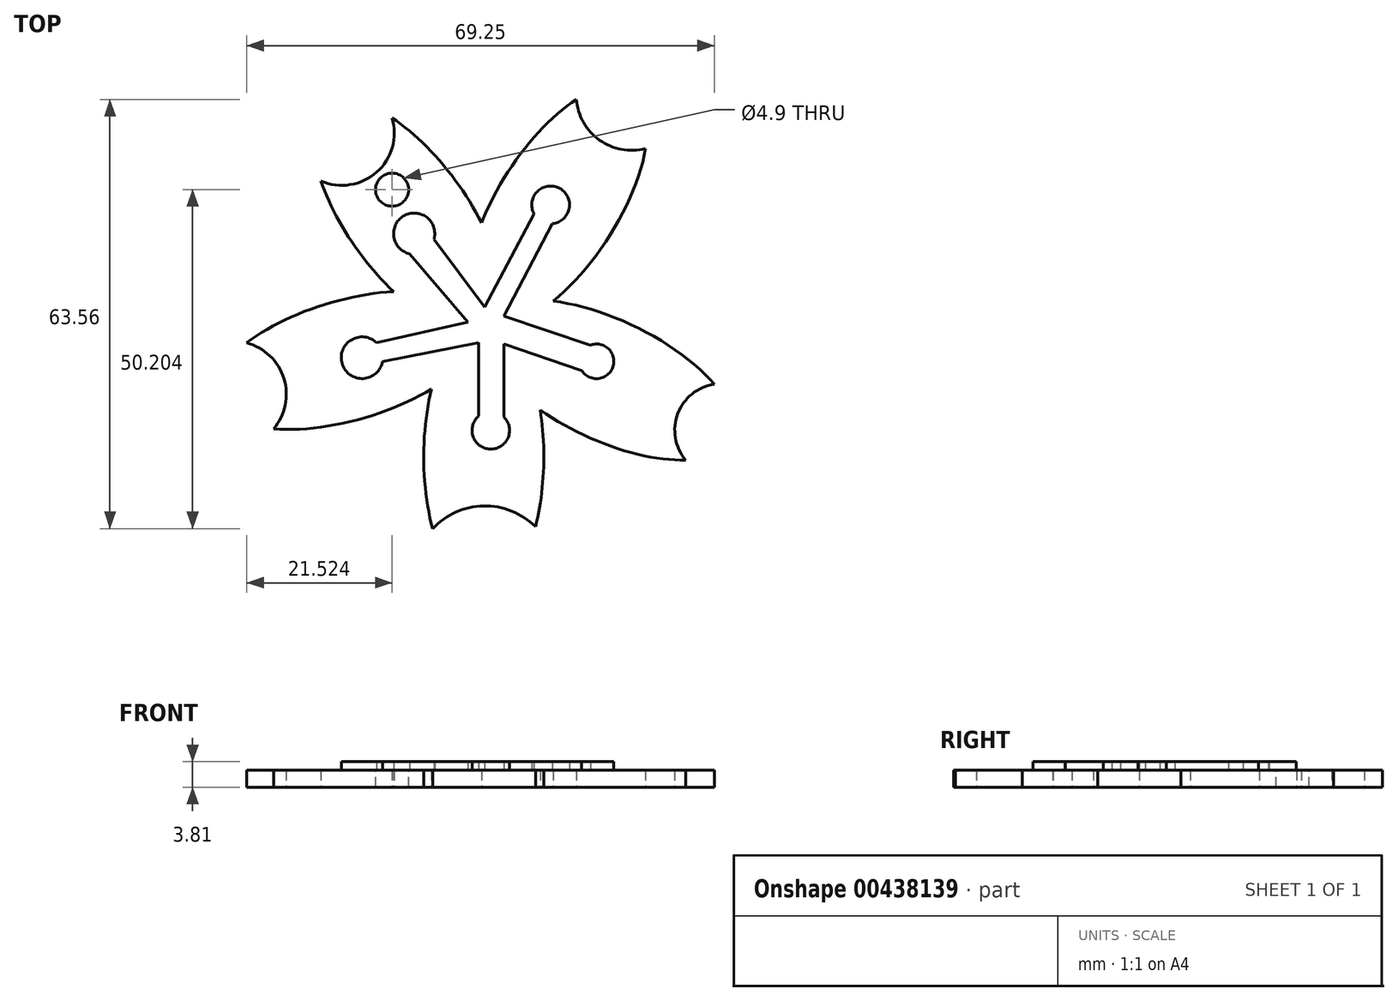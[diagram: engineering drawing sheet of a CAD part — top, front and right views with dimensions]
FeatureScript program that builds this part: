
annotation { "Feature Type Name" : "Feature", "Feature Type Description" : "" }
export const myFeature = defineFeature(function(context is Context, id is Id, definition is map)
    precondition{}
    {
        {
            var Q0;
            Q0=qCreatedBy(makeId("Top.planeOp"),FACE);
            var sketch = newSketch(context, id + "F0", { "sketchPlane" : qUnion([Q0])});
            skPoint(sketch, "E0.0.midPoint", {"position": v(-18.42, 2.19) * mm});
            skEllipticalArc(sketch, "E1", {});
            skArc(sketch, "E2", {"start": v(-10.76, -19.54) * mm, "mid": v(-18.44, -16.48) * mm, "end": v(-26, -19.84) * mm});
            skEllipticalArc(sketch, "E3", {});
            skArc(sketch, "E4", {"start": v(15.73, 1.54) * mm, "mid": v(10.31, -2.82) * mm, "end": v(11.48, -9.67) * mm});
            skEllipticalArc(sketch, "E5", {});
            skArc(sketch, "E6", {"start": v(-4.7, 43.72) * mm, "mid": v(-1.27, 37.7) * mm, "end": v(5.54, 36.44) * mm});
            skEllipticalArc(sketch, "E7", {});
            skArc(sketch, "E8", {"start": v(-42.53, 31.66) * mm, "mid": v(-34.28, 32.96) * mm, "end": v(-32, 41) * mm});
            skEllipticalArc(sketch, "E9", {});
            skArc(sketch, "E10", {"start": v(-49.56, -5.06) * mm, "mid": v(-48.02, 2.4) * mm, "end": v(-53.52, 7.67) * mm});
            skPoint(sketch, "E0.cCircle.center.orphan", {"position": v(-18.42, 10.93) * mm});
            skPoint(sketch, "E11.trimOffspring.end.orphan", {"position": v(-12.07, 2.19) * mm});
            skPoint(sketch, "E12.trimOffspring.end.orphan", {"position": v(-24.77, 2.19) * mm});
            const initialGuessF0  = {"E1": [-0.018419569358229637, -0.009209784679114819, 0, -1, 0.02032, 0.00889, 1.0375960775229152, 5.262947220574454], "E3": [-7.52416357180769e-05, 0.002189779299485402, -0.902772033588167, 0.4301193501472418, 0.02032, 0.00889, 3.914449507509073, 2.4409470220273937], "E5": [-0.0074550958280823094, 0.028037776911064273, -0.5395902327828408, -0.8419277764068362, 0.02032, 0.00889, 3.9042333142509738, 2.3368799745310973], "E7": [-0.029716556891798973, 0.026384949684143066, 0.5901133935646233, -0.8073203718076511, 0.02032, 0.00889, 4.0918939551895885, 2.2747363454446012], "E9": [-0.038638535887002945, 0.005087323021143675, 0.9606958523615047, 0.2776030966243028, 0.02032, 0.00889, 3.9984789776767142, 2.3025399142686345]};
            skSetInitialGuess(sketch, initialGuessF0);
            skSolve(sketch);
        }
        {
            var Q0;
            {var subQ0=sQuery(id+"F0.wireOp",EDGE,"E6");Q0=makeQuery(id+"F0.imprint","IMPRINT",FACE,{"disambiguationData":[TD([[makeQuery(id+"F0.imprint","IMPRINT",EDGE,{"derivedFrom":subQ0}),-1.0]])]});}
            var Q1;
            {var subQ0=sQuery(id+"F0.wireOp",EDGE,"E3");var subQ1=sQuery(id+"F0.wireOp",EDGE,"E1");var subQ2=makeQuery(id+"F0.imprint","INTERSECT",VERTEX,{"disambiguationData":[OD(1.0)],"derivedFrom":[subQ1,subQ0]});Q1=makeQuery(id+"F0.imprint","IMPRINT",FACE,{"disambiguationData":[TD([[makeQuery(id+"F0.imprint","IMPRINT",EDGE,{"disambiguationData":[TD([[subQ2,-1.0]])],"derivedFrom":subQ1}),-1.0]])]});}
            var Q2;
            {var subQ0=sQuery(id+"F0.wireOp",EDGE,"E8");Q2=makeQuery(id+"F0.imprint","IMPRINT",FACE,{"disambiguationData":[TD([[makeQuery(id+"F0.imprint","IMPRINT",EDGE,{"derivedFrom":subQ0}),-1.0]])]});}
            var Q3;
            {var subQ0=sQuery(id+"F0.wireOp",EDGE,"E10");Q3=makeQuery(id+"F0.imprint","IMPRINT",FACE,{"disambiguationData":[TD([[makeQuery(id+"F0.imprint","IMPRINT",EDGE,{"derivedFrom":subQ0}),-1.0]])]});}
            var Q4;
            {var subQ5=sQuery(id+"F0.wireOp",EDGE,"E2");Q4=makeQuery(id+"F0.imprint","IMPRINT",FACE,{"disambiguationData":[TD([[makeQuery(id+"F0.imprint","IMPRINT",EDGE,{"derivedFrom":subQ5}),-1.0]])]});}
            var Q5;
            {var subQ0=sQuery(id+"F0.wireOp",EDGE,"E4");Q5=makeQuery(id+"F0.imprint","IMPRINT",FACE,{"disambiguationData":[TD([[makeQuery(id+"F0.imprint","IMPRINT",EDGE,{"derivedFrom":subQ0}),-1.0]])]});}
            var Q6;
            {var subQ0=sQuery(id+"F0.wireOp",EDGE,"E3");var subQ1=sQuery(id+"F0.wireOp",EDGE,"E1");var subQ2=makeQuery(id+"F0.imprint","INTERSECT",VERTEX,{"disambiguationData":[OD(0.0)],"derivedFrom":[subQ1,subQ0]});Q6=makeQuery(id+"F0.imprint","IMPRINT",FACE,{"disambiguationData":[TD([[makeQuery(id+"F0.imprint","IMPRINT",EDGE,{"disambiguationData":[TD([[subQ2,-1.0]])],"derivedFrom":subQ1}),1.0]])]});}
            var Q7;
            {var subQ0=sQuery(id+"F0.wireOp",EDGE,"E5");var subQ1=sQuery(id+"F0.wireOp",EDGE,"E1");var subQ2=makeQuery(id+"F0.imprint","INTERSECT",VERTEX,{"disambiguationData":[OD(0.0)],"derivedFrom":[subQ1,subQ0]});Q7=makeQuery(id+"F0.imprint","IMPRINT",FACE,{"disambiguationData":[TD([[makeQuery(id+"F0.imprint","IMPRINT",EDGE,{"disambiguationData":[TD([[subQ2,-1.0]])],"derivedFrom":subQ1}),-1.0]])]});}
            var Q8;
            {var subQ0=sQuery(id+"F0.wireOp",EDGE,"E9");var subQ1=sQuery(id+"F0.wireOp",EDGE,"E1");var subQ2=makeQuery(id+"F0.imprint","INTERSECT",VERTEX,{"disambiguationData":[OD(1.0)],"derivedFrom":[subQ1,subQ0]});Q8=makeQuery(id+"F0.imprint","IMPRINT",FACE,{"disambiguationData":[TD([[makeQuery(id+"F0.imprint","IMPRINT",EDGE,{"disambiguationData":[TD([[subQ2,1.0]])],"derivedFrom":subQ1}),1.0]])]});}
            var Q9;
            {var subQ0=sQuery(id+"F0.wireOp",EDGE,"E9");var subQ1=sQuery(id+"F0.wireOp",EDGE,"E1");var subQ2=makeQuery(id+"F0.imprint","INTERSECT",VERTEX,{"disambiguationData":[OD(0.0)],"derivedFrom":[subQ1,subQ0]});Q9=makeQuery(id+"F0.imprint","IMPRINT",FACE,{"disambiguationData":[TD([[makeQuery(id+"F0.imprint","IMPRINT",EDGE,{"disambiguationData":[TD([[subQ2,-1.0]])],"derivedFrom":subQ1}),-1.0]])]});}
            var Q10;
            {var subQ0=sQuery(id+"F0.wireOp",EDGE,"E9");var subQ1=sQuery(id+"F0.wireOp",EDGE,"E1");var subQ2=makeQuery(id+"F0.imprint","INTERSECT",VERTEX,{"disambiguationData":[OD(0.0)],"derivedFrom":[subQ1,subQ0]});Q10=makeQuery(id+"F0.imprint","IMPRINT",FACE,{"disambiguationData":[TD([[makeQuery(id+"F0.imprint","IMPRINT",EDGE,{"disambiguationData":[TD([[subQ2,-1.0]])],"derivedFrom":subQ1}),1.0]])]});}
            var Q11;
            {var subQ0=sQuery(id+"F0.wireOp",EDGE,"E7");var subQ1=sQuery(id+"F0.wireOp",EDGE,"E1");var subQ2=makeQuery(id+"F0.imprint","INTERSECT",VERTEX,{"disambiguationData":[OD(0.0)],"derivedFrom":[subQ1,subQ0]});Q11=makeQuery(id+"F0.imprint","IMPRINT",FACE,{"disambiguationData":[TD([[makeQuery(id+"F0.imprint","IMPRINT",EDGE,{"disambiguationData":[TD([[subQ2,-1.0]])],"derivedFrom":subQ1}),-1.0]])]});}
            var Q12;
            {var subQ0=sQuery(id+"F0.wireOp",EDGE,"E7");var subQ1=sQuery(id+"F0.wireOp",EDGE,"E1");var subQ2=makeQuery(id+"F0.imprint","INTERSECT",VERTEX,{"disambiguationData":[OD(0.0)],"derivedFrom":[subQ1,subQ0]});Q12=makeQuery(id+"F0.imprint","IMPRINT",FACE,{"disambiguationData":[TD([[makeQuery(id+"F0.imprint","IMPRINT",EDGE,{"disambiguationData":[TD([[subQ2,-1.0]])],"derivedFrom":subQ1}),1.0]])]});}
            var Q13;
            {var subQ0=sQuery(id+"F0.wireOp",EDGE,"E5");var subQ1=sQuery(id+"F0.wireOp",EDGE,"E3");var subQ2=makeQuery(id+"F0.imprint","INTERSECT",VERTEX,{"disambiguationData":[OD(0.0)],"derivedFrom":[subQ1,subQ0]});Q13=makeQuery(id+"F0.imprint","IMPRINT",FACE,{"disambiguationData":[TD([[makeQuery(id+"F0.imprint","IMPRINT",EDGE,{"disambiguationData":[TD([[subQ2,-1.0]])],"derivedFrom":subQ1}),1.0]])]});}
            var Q14;
            {var subQ3=sQuery(id+"F0.wireOp",EDGE,"E9");var subQ7=sQuery(id+"F0.wireOp",EDGE,"E1");var subQ9=makeQuery(id+"F0.imprint","INTERSECT",VERTEX,{"disambiguationData":[OD(0.0)],"derivedFrom":[subQ7,subQ3]});Q14=makeQuery(id+"F0.imprint","IMPRINT",FACE,{"disambiguationData":[TD([[makeQuery(id+"F0.imprint","IMPRINT",EDGE,{"disambiguationData":[TD([[subQ9,1.0]])],"derivedFrom":subQ7}),1.0]])]});}
            var Q15;
            {var subQ0=sQuery(id+"F0.wireOp",EDGE,"E5");var subQ1=sQuery(id+"F0.wireOp",EDGE,"E1");var subQ2=makeQuery(id+"F0.imprint","INTERSECT",VERTEX,{"disambiguationData":[OD(0.0)],"derivedFrom":[subQ1,subQ0]});Q15=makeQuery(id+"F0.imprint","IMPRINT",FACE,{"disambiguationData":[TD([[makeQuery(id+"F0.imprint","IMPRINT",EDGE,{"disambiguationData":[TD([[subQ2,-1.0]])],"derivedFrom":subQ1}),1.0]])]});}
            var Q16;
            {var subQ0=sQuery(id+"F0.wireOp",EDGE,"E3");var subQ1=sQuery(id+"F0.wireOp",EDGE,"E1");var subQ2=makeQuery(id+"F0.imprint","INTERSECT",VERTEX,{"disambiguationData":[OD(1.0)],"derivedFrom":[subQ1,subQ0]});Q16=makeQuery(id+"F0.imprint","IMPRINT",FACE,{"disambiguationData":[TD([[makeQuery(id+"F0.imprint","IMPRINT",EDGE,{"disambiguationData":[TD([[subQ2,-1.0]])],"derivedFrom":subQ1}),1.0]])]});}
            extrude(context, id + "F1", {"entities" : qUnion([Q0, Q1, Q2, Q3, Q4, Q5, Q6, Q7, Q8, Q9, Q10, Q11, Q12, Q13, Q14, Q15, Q16]), "depth" : 2.54 * mm});
        }
        {
            var Q0;
            Q0=makeQuery(id+"F1.opExtrude","CAP_FACE",FACE,{"disambiguationData":[OSD([sQuery(id+"F0.wireOp",EDGE,"E1"),sQuery(id+"F0.wireOp",EDGE,"E2"),sQuery(id+"F0.wireOp",EDGE,"E3"),sQuery(id+"F0.wireOp",EDGE,"E4"),sQuery(id+"F0.wireOp",EDGE,"E5"),sQuery(id+"F0.wireOp",EDGE,"E6"),sQuery(id+"F0.wireOp",EDGE,"E7"),sQuery(id+"F0.wireOp",EDGE,"E8"),sQuery(id+"F0.wireOp",EDGE,"E9"),sQuery(id+"F0.wireOp",EDGE,"E10")])],"isStart":false});
            var sketch = newSketch(context, id + "F2", { "sketchPlane" : qUnion([Q0])});
            skCircle(sketch, "E13", {"center": v(-32, 30.36) * mm, "radius": 2.45 * mm});
            skPoint(sketch, "E14.center.orphan", {"position": v(-32, 30.78) * mm});
            skSolve(sketch);
        }
        {
            var Q0;
            Q0=makeQuery(id+"F2.imprint","IMPRINT",FACE,{"disambiguationData":[TD([[makeQuery(id+"F2.imprint","IMPRINT",EDGE,{"derivedFrom":sQuery(id+"F2.wireOp",EDGE,"E13")}),1.0]])]});
            extrude(context, id + "F3", {"entities" : qUnion([Q0]), "operationType" : NewBodyOperationType.REMOVE, "oppositeDirection" : true, "depth" : 25.4 * mm});
        }
        {
            var Q0;
            Q0=makeQuery(id+"F1.opExtrude","CAP_FACE",FACE,{"disambiguationData":[OSD([sQuery(id+"F0.wireOp",EDGE,"E1"),sQuery(id+"F0.wireOp",EDGE,"E2"),sQuery(id+"F0.wireOp",EDGE,"E3"),sQuery(id+"F0.wireOp",EDGE,"E4"),sQuery(id+"F0.wireOp",EDGE,"E5"),sQuery(id+"F0.wireOp",EDGE,"E6"),sQuery(id+"F0.wireOp",EDGE,"E7"),sQuery(id+"F0.wireOp",EDGE,"E8"),sQuery(id+"F0.wireOp",EDGE,"E9"),sQuery(id+"F0.wireOp",EDGE,"E10")])],"isStart":false});
            var sketch = newSketch(context, id + "F4", { "sketchPlane" : qUnion([Q0])});
            skLineSegment(sketch, "E15", {"start": v(-10.96, 26.77) * mm, "end": v(-18.3, 12.95) * mm});
            skLineSegment(sketch, "E16", {"start": v(-8.23, 25.33) * mm, "end": v(-15.42, 11.66) * mm});
            skLineSegment(sketch, "E17", {"start": v(-2.62, 7.34) * mm, "end": v(-15.42, 11.66) * mm});
            skLineSegment(sketch, "E18", {"start": v(-3.91, 3.6) * mm, "end": v(-15.42, 7.48) * mm});
            skLineSegment(sketch, "E19", {"start": v(-15.42, -3.3) * mm, "end": v(-15.42, 7.48) * mm});
            skLineSegment(sketch, "E20", {"start": v(-19.16, -3.17) * mm, "end": v(-19.16, 7.67) * mm});
            skLineSegment(sketch, "E21", {"start": v(-33.41, 4.9) * mm, "end": v(-19.16, 7.67) * mm});
            skLineSegment(sketch, "E22", {"start": v(-34.27, 7.67) * mm, "end": v(-20.75, 10.73) * mm});
            skPoint(sketch, "E22.endSnap0", {"position": v(-19.12, 10.73) * mm});
            skLineSegment(sketch, "E23", {"start": v(-29.38, 20.87) * mm, "end": v(-20.75, 10.73) * mm});
            skLineSegment(sketch, "E24", {"start": v(-25.78, 23.02) * mm, "end": v(-18.3, 12.95) * mm});
            skArc(sketch, "E25", {"start": v(-8.23, 25.33) * mm, "mid": v(-7.2, 30.58) * mm, "end": v(-10.96, 26.77) * mm});
            skArc(sketch, "E26", {"start": v(-3.91, 3.6) * mm, "mid": v(0.7, 4.1) * mm, "end": v(-2.62, 7.34) * mm});
            skArc(sketch, "E27", {"start": v(-19.16, -3.17) * mm, "mid": v(-17.48, -8.06) * mm, "end": v(-15.42, -3.3) * mm});
            skArc(sketch, "E28", {"start": v(-34.27, 7.67) * mm, "mid": v(-39.39, 4.56) * mm, "end": v(-33.41, 4.9) * mm});
            skArc(sketch, "E29", {"start": v(-25.78, 23.02) * mm, "mid": v(-30.3, 26.47) * mm, "end": v(-29.38, 20.87) * mm});
            skSolve(sketch);
        }
        {
            var Q0;
            Q0=makeQuery(id+"F4.imprint","IMPRINT",FACE,{"disambiguationData":[TD([[makeQuery(id+"F4.imprint","IMPRINT",EDGE,{"derivedFrom":sQuery(id+"F4.wireOp",EDGE,"E15")}),1.0]])]});
            extrude(context, id + "F5", {"entities" : qUnion([Q0]), "operationType" : NewBodyOperationType.ADD, "depth" : 1.27 * mm});
        }
    });
